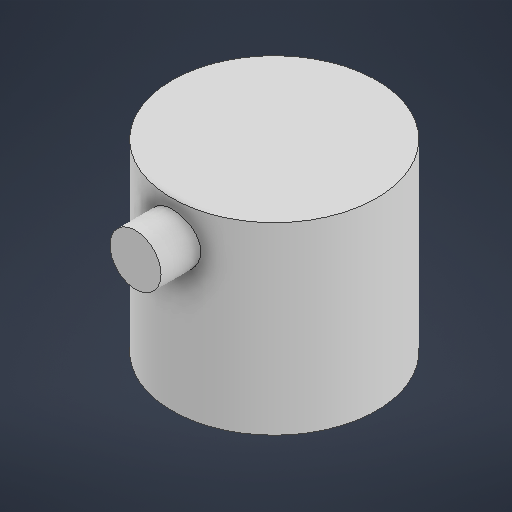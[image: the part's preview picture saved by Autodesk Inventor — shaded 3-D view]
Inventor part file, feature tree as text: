
AUTODESK INVENTOR PART (.ipt)
format: ipt  version: 2025 (Build 290162000, 162)  size: 177,152 bytes
history: native  units: in
note: dims shown in document units (in); Inventor stores cm internally (conversion verified against a paired STEP export)
features: extrude x2, sketch x2
ambient origin geometry x8: Origin, YZ Plane, XZ Plane, XY Plane, X Axis, Y Axis, Z Axis, Center Point
bodies: Solid1 (feature_tree)
feature tree (4):
  extrude  "Extrusion1"  Depth=0.63in TaperAngle=0.0deg
  extrude  "Extrusion2"  Depth=0.175in
  sketch  "Sketch1"  dims[d0=0.7in d1=0.63in d2=0.0in]
  sketch  "Sketch2"  dims[d3=0.12in d4=0.175in d5=0.475in d6=0.0in]
